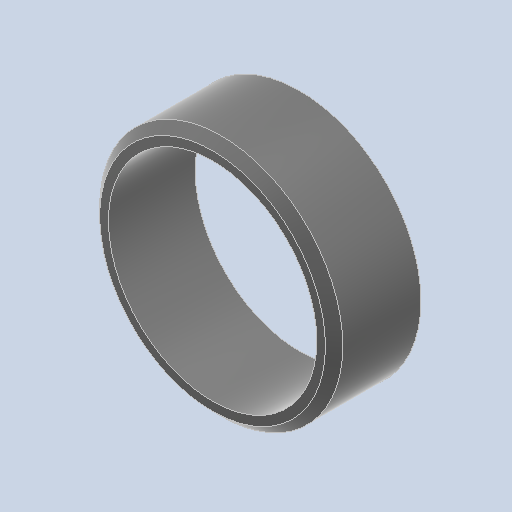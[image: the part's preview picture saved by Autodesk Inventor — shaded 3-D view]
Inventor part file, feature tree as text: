
AUTODESK INVENTOR PART (.ipt)
format: ipt  version: 2023 (Build 270158030, 158C)  size: 114,176 bytes
history: native  units: mm
features: other x3, sketch x1
ambient origin geometry x8: Origin, YZ Plane, XZ Plane, XY Plane, X Axis, Y Axis, Z Axis, Center Point
bodies: Solid1 (feature_tree)
feature tree (4):
  other  "w5f12-14n.ipt"
  other  "Solid1::w5f12-14n.ipt"
  other  "TaggingFeature1"
  sketch  "Sketch1"  dims[d0=10.0mm]
